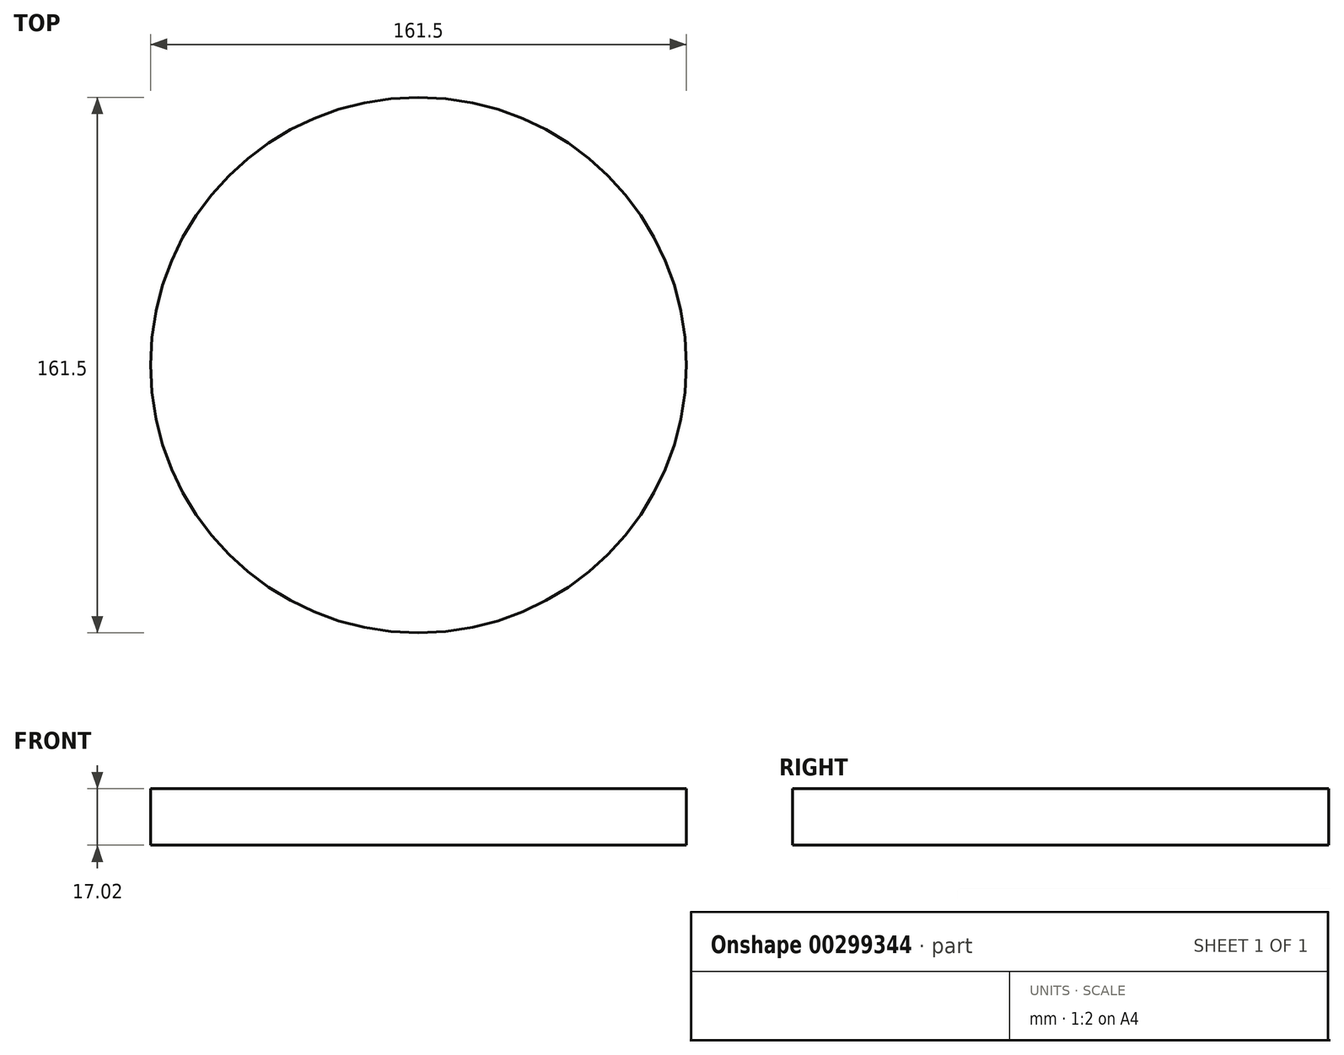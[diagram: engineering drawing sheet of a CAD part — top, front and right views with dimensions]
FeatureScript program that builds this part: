
annotation { "Feature Type Name" : "Feature", "Feature Type Description" : "" }
export const myFeature = defineFeature(function(context is Context, id is Id, definition is map)
    precondition{}
    {
        {
            var Q0;
            Q0=qCreatedBy(makeId("Top.planeOp"),FACE);
            var sketch = newSketch(context, id + "F0", { "sketchPlane" : qUnion([Q0])});
            skCircle(sketch, "E0", {"center": v(0, 0) * mm, "radius": 80.75 * mm});
            skSolve(sketch);
        }
        {
            var Q0;
            Q0 = qSketchRegion(id + "F0", true);
            extrude(context, id + "F1", {"entities" : qUnion([Q0]), "depth" : 17.02 * mm, "symmetric" : true});
        }
    });
